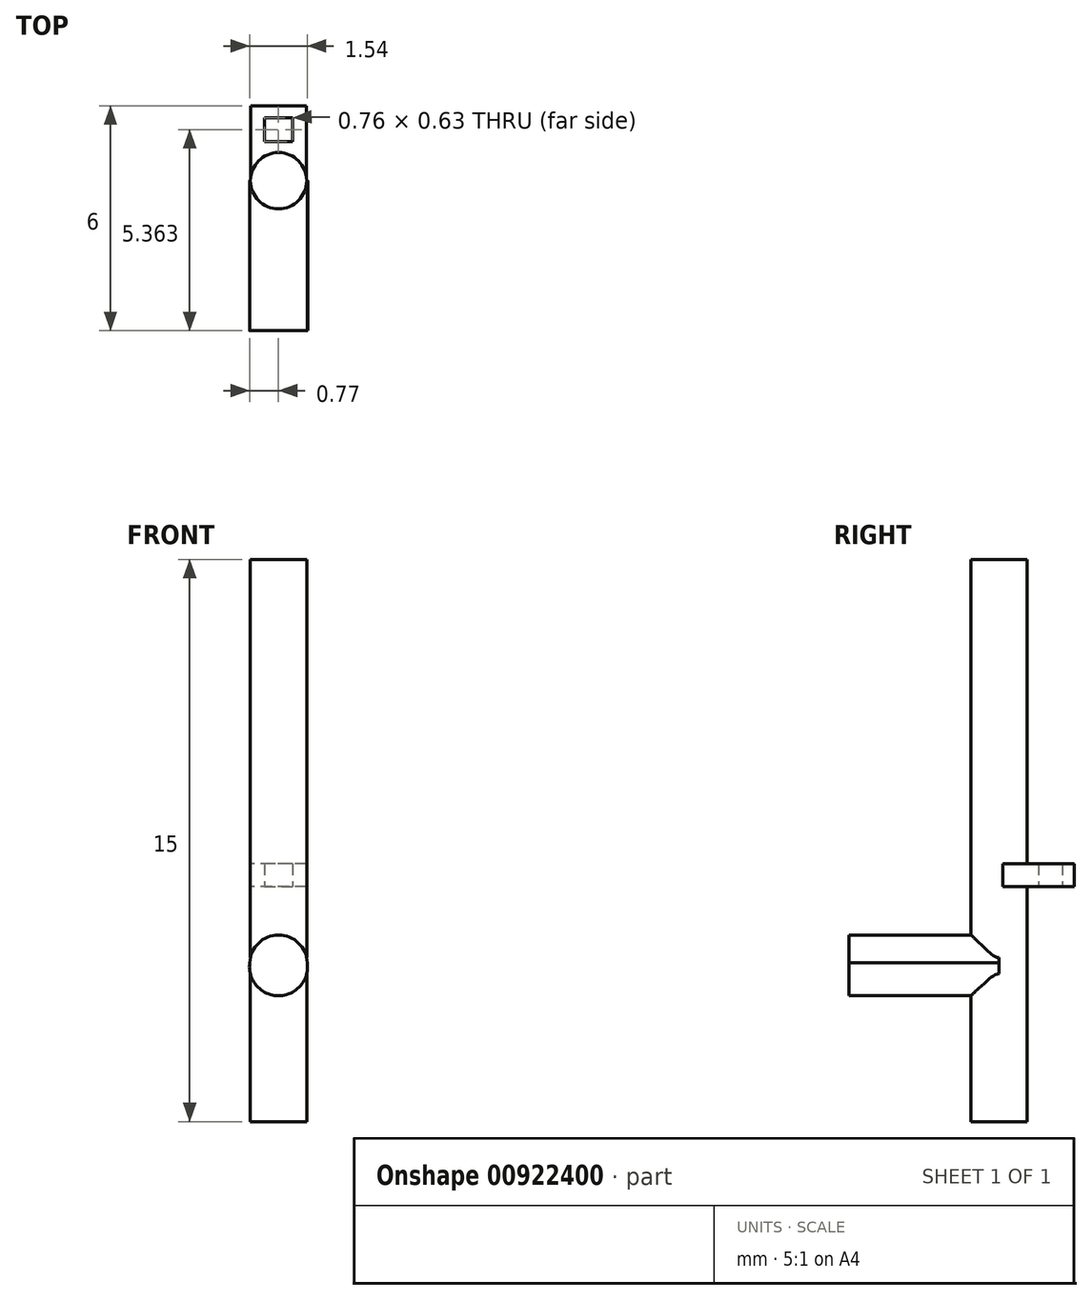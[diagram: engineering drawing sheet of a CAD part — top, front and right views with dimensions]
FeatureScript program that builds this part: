
annotation { "Feature Type Name" : "Feature", "Feature Type Description" : "" }
export const myFeature = defineFeature(function(context is Context, id is Id, definition is map)
    precondition{}
    {
        {
            var Q0;
            Q0=qCreatedBy(makeId("Top.planeOp"),FACE);
            var sketch = newSketch(context, id + "F0", { "sketchPlane" : qUnion([Q0])});
            skCircle(sketch, "E0", {"center": v(0, 0) * mm, "radius": 0.75 * mm});
            skSolve(sketch);
        }
        {
            var Q0;
            Q0=qSketchRegion(id+"F0",true);
            var Q1;
            Q1=makeQuery(id+"F0.imprint","IMPRINT",FACE,{"disambiguationData":[TD([[makeQuery(id+"F0.imprint","IMPRINT",EDGE,{"derivedFrom":sQuery(id+"F0.wireOp",EDGE,"E0")}),1.0]])]});
            extrude(context, id + "F1", {"entities" : qUnion([Q0, Q1]), "depth" : 15 * mm});
        }
        {
            var Q0;
            Q0=qCreatedBy(makeId("Front.planeOp"),FACE);
            var sketch = newSketch(context, id + "F2", { "sketchPlane" : qUnion([Q0])});
            skCircle(sketch, "E1", {"center": v(0, 4.2) * mm, "radius": 0.77 * mm});
            skSolve(sketch);
        }
        {
            var Q0;
            Q0=qSketchRegion(id+"F2",true);
            extrude(context, id + "F3", {"entities" : qUnion([Q0]), "operationType" : NewBodyOperationType.ADD, "depth" : 4 * mm});
        }
        {
            var Q0;
            Q0=qCreatedBy(makeId("Front.planeOp"),FACE);
            var sketch = newSketch(context, id + "F4", { "sketchPlane" : qUnion([Q0])});
            skCircle(sketch, "E2", {"center": v(0, 4.13) * mm, "radius": 0.77 * mm});
            skSolve(sketch);
        }
        {
            var Q0;
            Q0=qSketchRegion(id+"F4",true);
            extrude(context, id + "F5", {"entities" : qUnion([Q0]), "operationType" : NewBodyOperationType.ADD, "depth" : 4 * mm});
        }
        {
            var Q0;
            Q0=qCreatedBy(makeId("Front.planeOp"),FACE);
            var sketch = newSketch(context, id + "F6", { "sketchPlane" : qUnion([Q0])});
            skLineSegment(sketch, "E3.bottom", {"start": v(0.74, 6.87) * mm, "end": v(-0.74, 6.87) * mm});
            skLineSegment(sketch, "E3.top", {"start": v(0.74, 6.27) * mm, "end": v(-0.74, 6.27) * mm});
            skLineSegment(sketch, "E3.left", {"start": v(0.74, 6.87) * mm, "end": v(0.74, 6.27) * mm});
            skLineSegment(sketch, "E3.right", {"start": v(-0.74, 6.87) * mm, "end": v(-0.74, 6.27) * mm});
            skPoint(sketch, "E3.middle", {"position": v(0, 6.57) * mm});
            skSolve(sketch);
        }
        {
            var Q0;
            Q0=qSketchRegion(id+"F6",true);
            extrude(context, id + "F7", {"entities" : qUnion([Q0]), "operationType" : NewBodyOperationType.ADD, "oppositeDirection" : true, "depth" : 2 * mm});
        }
        {
            var Q0;
            Q0=makeQuery(id+"F7.opExtrude","SWEPT_FACE",FACE,{"disambiguationData":[OSD([sQuery(id+"F6.wireOp",EDGE,"E3.top")])]});
            var sketch = newSketch(context, id + "F8", { "sketchPlane" : qUnion([Q0])});
            skLineSegment(sketch, "E4.bottom", {"start": v(-0.38, -1.05) * mm, "end": v(0.38, -1.05) * mm});
            skLineSegment(sketch, "E4.top", {"start": v(-0.38, -1.68) * mm, "end": v(0.38, -1.68) * mm});
            skLineSegment(sketch, "E4.left", {"start": v(-0.38, -1.05) * mm, "end": v(-0.38, -1.68) * mm});
            skLineSegment(sketch, "E4.right", {"start": v(0.38, -1.05) * mm, "end": v(0.38, -1.68) * mm});
            skPoint(sketch, "E4.middle", {"position": v(0, -1.36) * mm});
            skPoint(sketch, "E4.cornerSnap0", {"position": v(-0.74, -1.05) * mm});
            skSolve(sketch);
        }
        {
            var Q0;
            Q0=qSketchRegion(id+"F8",true);
            extrude(context, id + "F9", {"entities" : qUnion([Q0]), "operationType" : NewBodyOperationType.REMOVE, "oppositeDirection" : true, "depth" : 25 * mm});
        }
    });
